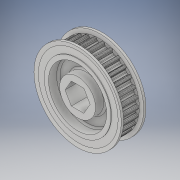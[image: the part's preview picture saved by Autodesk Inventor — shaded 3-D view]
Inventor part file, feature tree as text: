
AUTODESK INVENTOR PART (.ipt)
format: ipt  version: 2018 (Build 220112000, 112)  size: 929,280 bytes
history: native  units: in
note: dims shown in document units (in); Inventor stores cm internally (conversion verified against a paired STEP export)
features: mirror x1
ambient origin geometry x8: Origin, YZ Plane, XZ Plane, XY Plane, X Axis, Y Axis, Z Axis, Center Point
bodies: Solid1 (feature_tree)
feature tree (1):
  mirror  "Mirror1"
